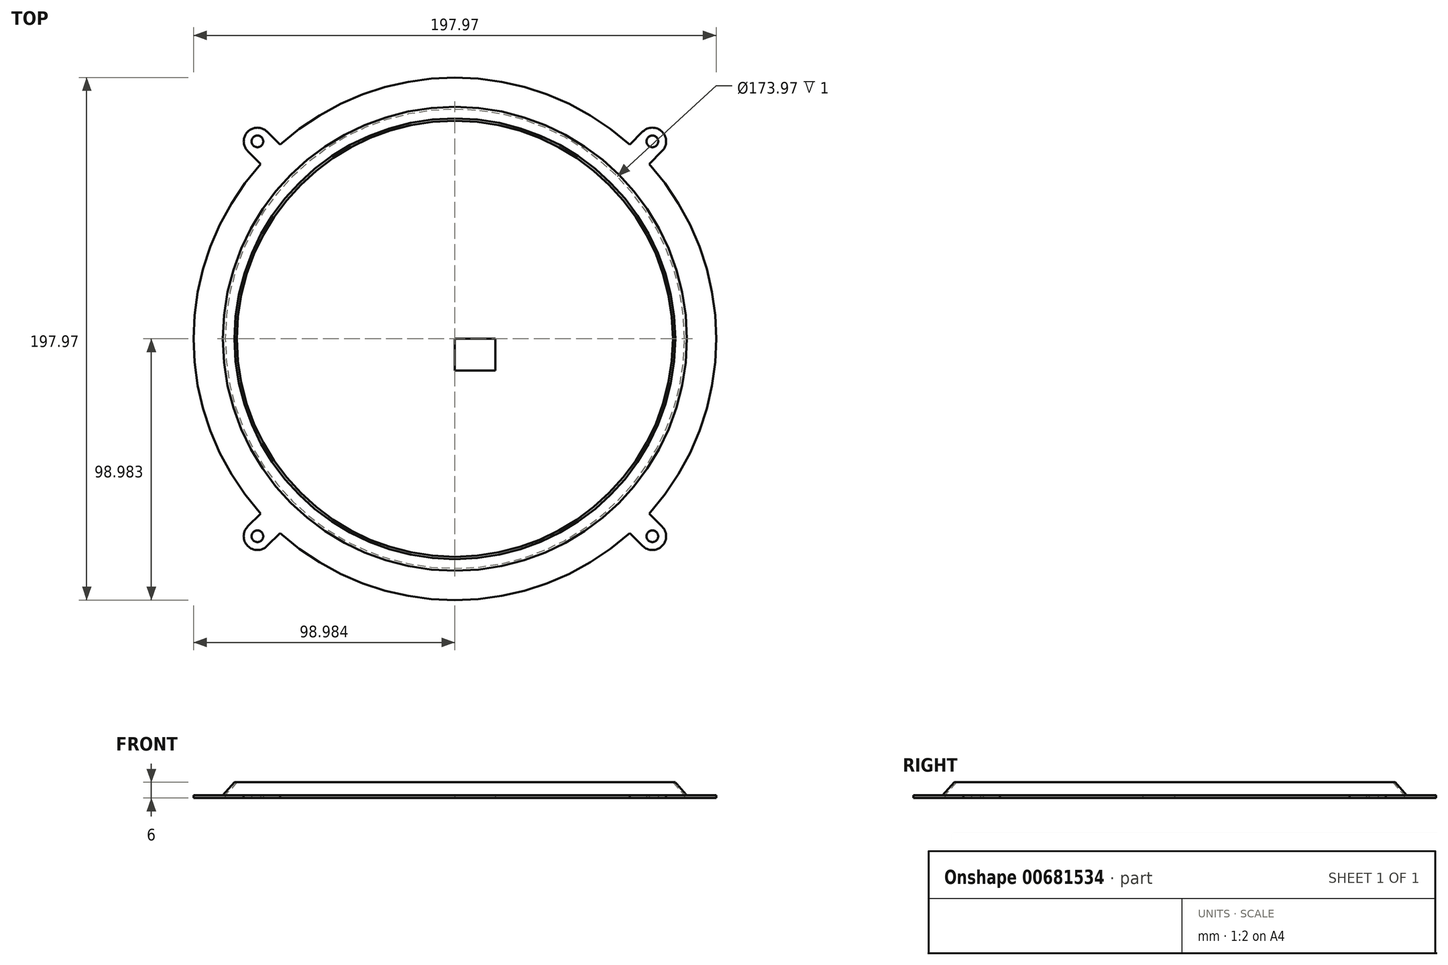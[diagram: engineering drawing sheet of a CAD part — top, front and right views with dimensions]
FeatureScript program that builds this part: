
annotation { "Feature Type Name" : "Feature", "Feature Type Description" : "" }
export const myFeature = defineFeature(function(context is Context, id is Id, definition is map)
    precondition{}
    {
        {
            var Q0;
            Q0=qCreatedBy(makeId("Top.planeOp"),FACE);
            var sketch = newSketch(context, id + "F0", { "sketchPlane" : qUnion([Q0])});
            skCircle(sketch, "E0", {"center": v(95.8, 90.85) * mm, "radius": 2.2 * mm});
            skArc(sketch, "E1", {"start": v(99.47, 87.18) * mm, "mid": v(99.47, 94.53) * mm, "end": v(92.12, 94.53) * mm});
            skLineSegment(sketch, "E2.bottom", {"start": v(92.12, 94.53) * mm, "end": v(87.21, 89.62) * mm});
            skLineSegment(sketch, "E2.top", {"start": v(99.47, 87.18) * mm, "end": v(94.57, 82.27) * mm});
            skPoint(sketch, "E2.middle", {"position": v(0, 0) * mm});
            skArc(sketch, "E3", {"start": v(107.98, 16.05) * mm, "mid": v(82.5, 77.56) * mm, "end": v(21, 103.04) * mm});
            skArc(sketch, "E4", {"start": v(87.21, 89.62) * mm, "mid": v(56.46, 108.47) * mm, "end": v(21, 115.04) * mm});
            skArc(sketch, "E5.trimOffspring", {"start": v(119.98, 16.05) * mm, "mid": v(113.4, 51.52) * mm, "end": v(94.57, 82.27) * mm});
            skLineSegment(sketch, "E6.left", {"start": v(21, 16.05) * mm, "end": v(21, 4.01) * mm});
            skLineSegment(sketch, "E7.MirrorCS", {"start": v(99.47, -55.07) * mm, "end": v(94.57, -50.17) * mm});
            skLineSegment(sketch, "E8.MirrorCS", {"start": v(92.12, -62.42) * mm, "end": v(87.21, -57.52) * mm});
            skCircle(sketch, "E9.MirrorC", {"center": v(95.8, -58.75) * mm, "radius": 2.2 * mm});
            skArc(sketch, "E10.MirrorCS", {"start": v(99.47, -55.07) * mm, "mid": v(99.47, -62.42) * mm, "end": v(92.12, -62.42) * mm});
            skLineSegment(sketch, "E11.MirrorCS", {"start": v(36.26, 16.05) * mm, "end": v(36.26, 4.01) * mm});
            skArc(sketch, "E12.MirrorCS", {"start": v(-57.48, -55.07) * mm, "mid": v(-57.48, -62.42) * mm, "end": v(-50.13, -62.42) * mm});
            skLineSegment(sketch, "E13.MirrorCS", {"start": v(-57.48, -55.07) * mm, "end": v(-52.58, -50.17) * mm});
            skLineSegment(sketch, "E14.MirrorCS", {"start": v(-50.13, -62.42) * mm, "end": v(-45.22, -57.52) * mm});
            skCircle(sketch, "E15.MirrorC", {"center": v(-53.8, -58.75) * mm, "radius": 2.2 * mm});
            skCircle(sketch, "E16.MirrorC", {"center": v(-53.8, 90.85) * mm, "radius": 2.2 * mm});
            skLineSegment(sketch, "E17.MirrorCS", {"start": v(-50.13, 94.53) * mm, "end": v(-45.22, 89.62) * mm});
            skLineSegment(sketch, "E18.MirrorCS", {"start": v(-57.48, 87.18) * mm, "end": v(-52.58, 82.27) * mm});
            skLineSegment(sketch, "E19.MirrorCS", {"start": v(21, 16.05) * mm, "end": v(36.26, 16.05) * mm});
            skLineSegment(sketch, "E20.MirrorCS", {"start": v(21, 4.01) * mm, "end": v(36.26, 4.01) * mm});
            skArc(sketch, "E21.MirrorCS", {"start": v(-57.48, 87.18) * mm, "mid": v(-57.48, 94.53) * mm, "end": v(-50.13, 94.53) * mm});
            skPoint(sketch, "E22.MirrorCS.start.orphan", {"position": v(107.98, 16.05) * mm});
            skPoint(sketch, "E23.MirrorCS.start.orphan", {"position": v(119.98, 16.05) * mm});
            skCircle(sketch, "E24", {"center": v(21, 16.05) * mm, "radius": 86.98 * mm});
            skArc(sketch, "E25", {"start": v(-45.22, -57.52) * mm, "mid": v(21, -82.93) * mm, "end": v(87.21, -57.52) * mm});
            skArc(sketch, "E26.trimOffspring", {"start": v(-52.58, 82.27) * mm, "mid": v(-77.99, 16.05) * mm, "end": v(-52.58, -50.17) * mm});
            skArc(sketch, "E27.trimOffspring", {"start": v(94.57, -50.17) * mm, "mid": v(119.98, 16.05) * mm, "end": v(94.57, 82.27) * mm});
            skArc(sketch, "E28.trimOffspring", {"start": v(87.21, 89.62) * mm, "mid": v(21, 115.04) * mm, "end": v(-45.22, 89.62) * mm});
            skLineSegment(sketch, "E29", {"start": v(21, 115.04) * mm, "end": v(21, 103.04) * mm});
            skLineSegment(sketch, "E30", {"start": v(107.98, 16.05) * mm, "end": v(119.98, 16.05) * mm});
            skSolve(sketch);
        }
        {
            var Q0;
            Q0=makeQuery(id+"F0.imprint","IMPRINT",FACE,{"disambiguationData":[TD([[makeQuery(id+"F0.imprint","IMPRINT",EDGE,{"derivedFrom":sQuery(id+"F0.wireOp",EDGE,"E0")}),-1.0]])]});
            extrude(context, id + "F1", {"entities" : qUnion([Q0]), "depth" : 1 * mm, "offsetDistance" : 25 * mm});
        }
        {
            var Q0;
            Q0=makeQuery(id+"F1.opExtrude","SWEPT_FACE",FACE,{"disambiguationData":[OSD([sQuery(id+"F0.wireOp",EDGE,"E30")])]});
            var sketch = newSketch(context, id + "F2", { "sketchPlane" : qUnion([Q0])});
            skLineSegment(sketch, "E31", {"start": v(104.48, 6) * mm, "end": v(108.88, 1) * mm});
            skLineSegment(sketch, "E32", {"start": v(103.58, 6) * mm, "end": v(107.98, 1) * mm});
            skLineSegment(sketch, "E33", {"start": v(103.58, 6) * mm, "end": v(104.48, 6) * mm});
            skLineSegment(sketch, "E34", {"start": v(107.98, 1) * mm, "end": v(108.88, 1) * mm});
            skSolve(sketch);
        }
        {
            var Q0;
            {Q0=qUnion([makeQuery(id+"F0.imprint","IMPRINT",FACE,{"disambiguationData":[TD([[makeQuery(id+"F0.imprint","IMPRINT",EDGE,{"derivedFrom":sQuery(id+"F0.wireOp",EDGE,"E0")}),-1.0]])]}),makeQuery(id+"F0.imprint","IMPRINT",FACE,{"disambiguationData":[TD([[makeQuery(id+"F0.imprint","IMPRINT",EDGE,{"derivedFrom":sQuery(id+"F0.wireOp",EDGE,"E7.MirrorCS")}),1.0]])]})]);}
            var Q1;
            Q1=makeQuery(id+"F0.imprint","IMPRINT",FACE,{"disambiguationData":[TD([[makeQuery(id+"F0.imprint","IMPRINT",EDGE,{"derivedFrom":sQuery(id+"F0.wireOp",EDGE,"E6.left")}),1.0]])]});
            extrude(context, id + "F3", {"entities" : qUnion([Q0, Q1]), "operationType" : NewBodyOperationType.ADD, "depth" : 1 * mm, "offsetDistance" : 25 * mm});
        }
        {
            var Q0;
            Q0=makeQuery(id+"F2.imprint","IMPRINT",FACE,{"disambiguationData":[TD([[makeQuery(id+"F2.imprint","IMPRINT",EDGE,{"derivedFrom":sQuery(id+"F2.wireOp",EDGE,"E31")}),-1.0]])]});
            var Q1;
            Q1=makeQuery(id+"F3.opExtrude","SWEPT_EDGE",EDGE,{"disambiguationData":[OSD([sQuery(id+"F0.wireOp",EDGE,"E6.left"),sQuery(id+"F0.wireOp",EDGE,"E19.MirrorCS")])]});
            revolve(context, id + "F4", {"entities" : qUnion([Q0]), "axis" : qUnion([Q1]), "revolveType" : RevolveType.FULL});
        }
    });
